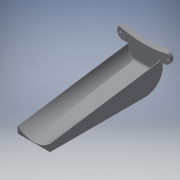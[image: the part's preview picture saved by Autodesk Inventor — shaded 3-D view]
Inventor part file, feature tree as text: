
AUTODESK INVENTOR PART (.ipt)
format: ipt  version: 2016 (Build 200138000, 138)  size: 299,008 bytes
history: native  units: mm
features: fillet x6, sketch x5, extrude x4, plane x2, loft x1, chamfer x1
ambient origin geometry x8: Origin, YZ Plane, XZ Plane, XY Plane, X Axis, Y Axis, Z Axis, Center Point
bodies: Solid1 (feature_tree)
feature tree (19):
  extrude  "Extrusion1"  Depth=60.0mm
  plane  "Work Plane1"
  extrude  "Extrusion2"  Depth=90.0mm TaperAngle=0.0deg
  plane  "Work Plane2"
  loft  "Loft4"
  extrude  "Extrusion3"  Depth=18.0mm
  fillet  "Fillet1"  Radius=190.0mm
  extrude  "Extrusion4"  Depth=10.0mm
  chamfer  "Chamfer2"  Distance=4.0mm
  fillet  "Fillet4"  Radius=40.0mm
  fillet  "Fillet5"  Radius=40.0mm
  fillet  "Fillet6"  Radius=10.0mm
  fillet  "Fillet7"  Radius=5.0mm
  fillet  "Fillet8"  Radius=10.0mm
  sketch  "Sketch1"  dims[d0=190.0mm d1=60.0mm]
  sketch  "Sketch2"  dims[d2=40.0mm d3=90.0mm d4=0.0mm]
  sketch  "Sketch3"  dims[d10=40.0mm d11=0.0mm d12=190.0mm]
  sketch  "Sketch6"  dims[d13=18.0mm d14=18.0mm d15=190.0mm]
  sketch  "Sketch7"  dims[d16=90.0deg d20=12.0mm d38=4.0mm d39=40.0mm d40=40.0mm d41=0.0mm d42=10.0mm d47=5.0mm d49=10.0mm d50=0.0mm d51=4.0mm d52=5.0mm d53=45.0deg d54=4.0mm d55=30.0mm d56=0.8mm d57=0.8mm d59=0.8mm d60=0.8mm d61=26.2mm d62=0.0mm d63=90.0deg d64=0.0mm d65=90.0deg d66=2.0mm d67=2.0mm d68=2.0mm d69=10.0mm]
